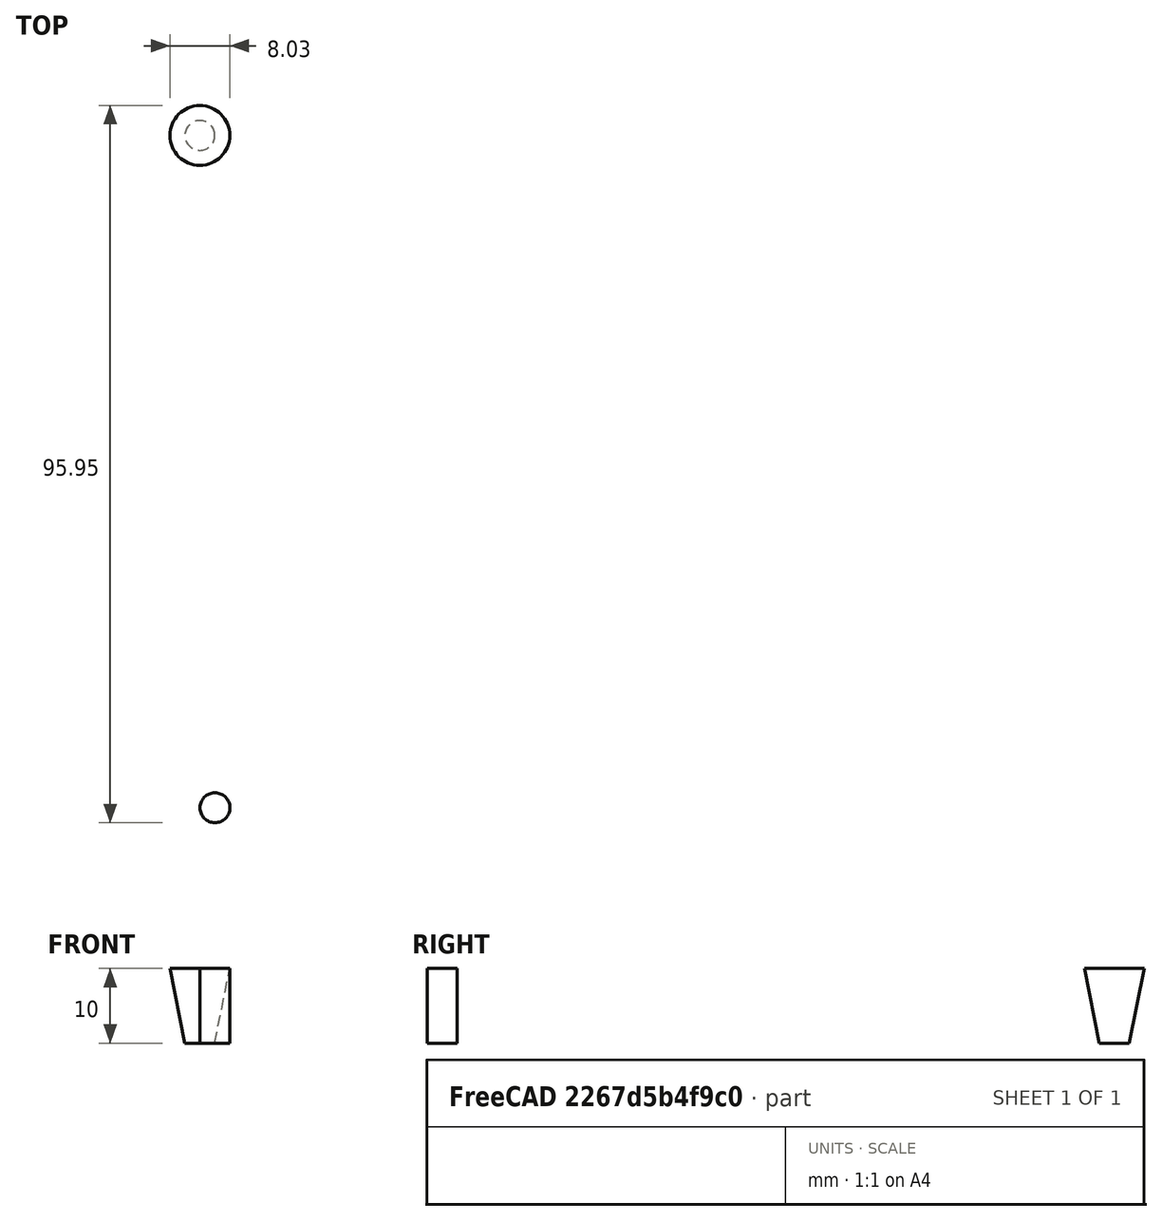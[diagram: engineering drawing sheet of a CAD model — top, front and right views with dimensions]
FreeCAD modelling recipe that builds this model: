
FCSTD DOCUMENT  (FreeCAD 0.19R)
Label: m04_auto2
License: All rights reserved
LicenseURL: http://en.wikipedia.org/wiki/All_rights_reserved
objects: Sketcher::SketchObject×3, Part::Part2DObjectPython×1, Part::Cone×1, Part::Cylinder×1
note: 6 computed .brp shape members not serialized (recipe doc carries the construction recipe); baked Part::Feature solids carry a one-line shape summary decoded from their .brp

FEATURE [Part::Part2DObjectPython] BSpline  # Draft 2D object (typed FeaturePython)
  Closed = false
  MakeFace = true
  Parameterization = 1
  Points = (4) [(-26.3062,80.0863,0),(-162.102,163.875,0),(-324.48,82.3977,0),(-520.951,155.208,0)]
FEATURE [Sketcher::SketchObject] Sketch021  label="Auto"
  Placement = pos=(-966.571,574.952,0) rot=(0,0,1;0.041689rad)
  sketch-geometry (8):
    g0: LineSegment StartX=6.62525 StartY=0.510051 StartZ=0 EndX=6.62525 EndY=-85.4899 EndZ=0
    g1: LineSegment StartX=6.62525 StartY=-85.4899 StartZ=0 EndX=-5.19676 EndY=-85.4899 EndZ=0
    g2: LineSegment StartX=-5.19676 StartY=-85.4899 StartZ=0 EndX=-5.19676 EndY=0.510051 EndZ=0
    g3: LineSegment StartX=-5.19676 StartY=0.510051 StartZ=0 EndX=6.62525 EndY=0.510051 EndZ=0
    g4: LineSegment StartX=-13.8484 StartY=6.1744 StartZ=0 EndX=13.4418 EndY=6.1744 EndZ=0
    g5: LineSegment StartX=13.4418 StartY=6.1744 StartZ=0 EndX=13.4418 EndY=-89.5335 EndZ=0
    g6: LineSegment StartX=13.4418 StartY=-89.5335 StartZ=0 EndX=-13.8484 EndY=-89.5335 EndZ=0
    g7: LineSegment StartX=-13.8484 StartY=-89.5335 StartZ=0 EndX=-13.8484 EndY=6.1744 EndZ=0
  constraints (17):
    c: Coincident(g0,g1)
    c: Coincident(g1,g2)
    c: Horizontal(g1)
    c: Vertical(g0)
    c: Vertical(g2)
    c: Coincident(g3,g2)
    c: Coincident(g3,g0)
    c: Horizontal(g3)
    c: DistanceY(g2,g2) = 86
    c: Coincident(g4,g5)
    c: Coincident(g5,g6)
    c: Coincident(g6,g7)
    c: Coincident(g7,g4)
    c: Horizontal(g4)
    c: Horizontal(g6)
    c: Vertical(g5)
    c: Vertical(g7)
FEATURE [Sketcher::SketchObject] Sketch  label="Path"
  sketch-geometry (7):
    g0-g3: Circle [constr] x4 (B-spline internal-alignment scaffolding for g4; pole/knot coordinates omitted)
    g4: BSplineCurve PolesCount=4 KnotsCount=2 Degree=3 IsPeriodic=0
    g5: GeomPoint [constr] X=-36.2426 Y=128.479 Z=0
    g6: GeomPoint [constr] X=-964.482 Y=804.112 Z=0
  constraints (7):
    c: Radius(g0) = 40
    c: Equal(g0,g1)
    c: Equal(g0,g2)
    c: Equal(g0,g3)
    c: InternalAlignment(g0-g3 -> g4) x4
    c: InternalAlignment(g5,g4)
    c: InternalAlignment(g6,g4)
FEATURE [Part::Cone] Cone
  Angle = 360
  AttacherType = Attacher::AttachEngine3D
  Height = 10
  Placement = pos=(-37.6964,328.08,0) rot=(0,0,1;0.022742rad)
  Radius1 = 2
  Radius2 = 4
FEATURE [Part::Cylinder] Cylinder
  Angle = 360
  AttacherType = Attacher::AttachEngine3D
  Height = 10
  Placement = pos=(-35.672,238.125,0) rot=(0,0,1;0.005754rad)
  Radius = 2
FEATURE [Sketcher::SketchObject] Sketch022  label="Auto001"
  Placement = pos=(-35.6783,237.765,0) rot=(0,0,1;0.002617rad)
  sketch-geometry (8):
    g0: LineSegment StartX=6.62525 StartY=0.510051 StartZ=0 EndX=6.62525 EndY=-85.4899 EndZ=0
    g1: LineSegment StartX=6.62525 StartY=-85.4899 StartZ=0 EndX=-5.19676 EndY=-85.4899 EndZ=0
    g2: LineSegment StartX=-5.19676 StartY=-85.4899 StartZ=0 EndX=-5.19676 EndY=0.510051 EndZ=0
    g3: LineSegment StartX=-5.19676 StartY=0.510051 StartZ=0 EndX=6.62525 EndY=0.510051 EndZ=0
    g4: LineSegment StartX=-13.8484 StartY=6.1744 StartZ=0 EndX=13.4418 EndY=6.1744 EndZ=0
    g5: LineSegment StartX=13.4418 StartY=6.1744 StartZ=0 EndX=13.4418 EndY=-89.5335 EndZ=0
    g6: LineSegment StartX=13.4418 StartY=-89.5335 StartZ=0 EndX=-13.8484 EndY=-89.5335 EndZ=0
    g7: LineSegment StartX=-13.8484 StartY=-89.5335 StartZ=0 EndX=-13.8484 EndY=6.1744 EndZ=0
  constraints (17):
    c: Coincident(g0,g1)
    c: Coincident(g1,g2)
    c: Horizontal(g1)
    c: Vertical(g0)
    c: Vertical(g2)
    c: Coincident(g3,g2)
    c: Coincident(g3,g0)
    c: Horizontal(g3)
    c: DistanceY(g2,g2) = 86
    c: Coincident(g4,g5)
    c: Coincident(g5,g6)
    c: Coincident(g6,g7)
    c: Coincident(g7,g4)
    c: Horizontal(g4)
    c: Horizontal(g6)
    c: Vertical(g5)
    c: Vertical(g7)
